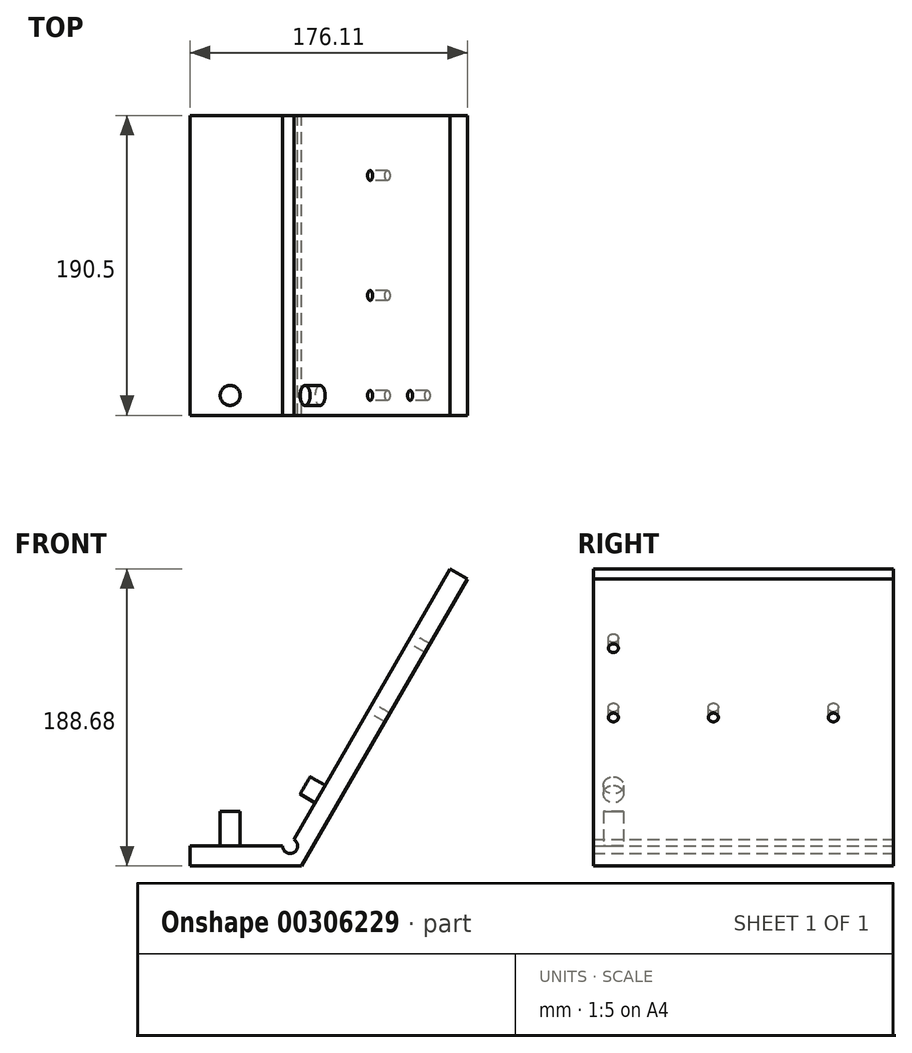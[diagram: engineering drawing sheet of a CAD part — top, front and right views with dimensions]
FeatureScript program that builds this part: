
annotation { "Feature Type Name" : "Feature", "Feature Type Description" : "" }
export const myFeature = defineFeature(function(context is Context, id is Id, definition is map)
    precondition{}
    {
        {
            var Q0;
            Q0=qCreatedBy(makeId("Front.planeOp"),FACE);
            var sketch = newSketch(context, id + "F0", { "sketchPlane" : qUnion([Q0])});
            skLineSegment(sketch, "E0", {"start": v(0, 0) * mm, "end": v(0, 12.7) * mm});
            skLineSegment(sketch, "E1", {"start": v(0, 12.7) * mm, "end": v(58.74, 12.7) * mm});
            skLineSegment(sketch, "E2", {"start": v(65.89, 16.82) * mm, "end": v(165.11, 188.68) * mm});
            skLineSegment(sketch, "E3", {"start": v(165.11, 188.68) * mm, "end": v(176.11, 182.33) * mm});
            skLineSegment(sketch, "E4", {"start": v(176.11, 182.33) * mm, "end": v(70.84, 0) * mm});
            skLineSegment(sketch, "E5", {"start": v(70.84, 0) * mm, "end": v(0, 0) * mm});
            skArc(sketch, "E6", {"start": v(58.74, 12.7) * mm, "mid": v(65.88, 8.57) * mm, "end": v(65.89, 16.82) * mm});
            skLineSegment(sketch, "E7.trimOffspring", {"start": v(63.5, 12.7) * mm, "end": v(63.5, 12.7) * mm});
            skSolve(sketch);
        }
        {
            var Q0;
            Q0 = qSketchRegion(id + "F0", true);
            extrude(context, id + "F1", {"entities" : qUnion([Q0]), "depth" : 190.5 * mm});
        }
        {
            var Q0;
            Q0=makeQuery(id+"F1.opExtrude","SWEPT_FACE",FACE,{"disambiguationData":[OSD([sQuery(id+"F0.wireOp",EDGE,"E2")])]});
            var sketch = newSketch(context, id + "F2", { "sketchPlane" : qUnion([Q0])});
            skCircle(sketch, "E8", {"center": v(38.1, 144.36) * mm, "radius": 3.18 * mm});
            skCircle(sketch, "E9", {"center": v(114.3, 144.36) * mm, "radius": 3.18 * mm});
            skCircle(sketch, "E10", {"center": v(177.8, 144.36) * mm, "radius": 3.18 * mm});
            skCircle(sketch, "E11", {"center": v(177.8, 195.16) * mm, "radius": 3.18 * mm});
            skSolve(sketch);
        }
        {
            var Q0;
            Q0 = qSketchRegion(id + "F2", true);
            extrude(context, id + "F3", {"entities" : qUnion([Q0]), "operationType" : NewBodyOperationType.REMOVE, "oppositeDirection" : true, "depth" : 25.4 * mm});
        }
        {
            var Q0;
            Q0=makeQuery(id+"F1.opExtrude","SWEPT_FACE",FACE,{"disambiguationData":[OSD([sQuery(id+"F0.wireOp",EDGE,"E2")])]});
            var sketch = newSketch(context, id + "F4", { "sketchPlane" : qUnion([Q0])});
            skCircle(sketch, "E12", {"center": v(177.8, 80.86) * mm, "radius": 6.35 * mm});
            skSolve(sketch);
        }
        {
            var Q0;
            Q0 = qSketchRegion(id + "F4", true);
            extrude(context, id + "F5", {"entities" : qUnion([Q0]), "operationType" : NewBodyOperationType.ADD, "depth" : 11 * mm});
        }
        {
            var Q0;
            Q0=makeQuery(id+"F1.opExtrude","SWEPT_FACE",FACE,{"disambiguationData":[OSD([sQuery(id+"F0.wireOp",EDGE,"E1")])]});
            var sketch = newSketch(context, id + "F6", { "sketchPlane" : qUnion([Q0])});
            skCircle(sketch, "E13", {"center": v(25.4, -177.8) * mm, "radius": 6.35 * mm});
            skSolve(sketch);
        }
        {
            var Q0;
            Q0 = qSketchRegion(id + "F6", true);
            extrude(context, id + "F7", {"entities" : qUnion([Q0]), "operationType" : NewBodyOperationType.ADD, "depth" : 22 * mm});
        }
    });
